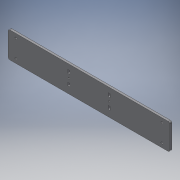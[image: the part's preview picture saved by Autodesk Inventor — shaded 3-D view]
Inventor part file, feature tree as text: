
AUTODESK INVENTOR PART (.ipt)
format: ipt  version: 2019 (Build 230136000, 136)  size: 161,280 bytes
history: native  units: in
note: dims shown in document units (in); Inventor stores cm internally (conversion verified against a paired STEP export)
features: reference x12, other x6, extrude x3, sketch x2, fillet x1, helix x1
ambient origin geometry x8: Origin, YZ Plane, XZ Plane, XY Plane, X Axis, Y Axis, Z Axis, Center Point
bodies: Solid1 (feature_tree)
feature tree (25):
  extrude  "Extrusion1"  Depth=0.1575in TaperAngle=0.0deg
  fillet  "Fillet1"  Radius=0.125in
  extrude  "Extrusion2"  Depth=0.1575in
  extrude  "Extrusion3"  Depth=0.1575in
  reference  "Reference1"
  sketch  "Sketch2"  dims[d0=1.9685in d1=0.1575in d2=0.0in d3=0.125in]
  reference  "Reference3"
  reference  "Reference4"
  reference  "Reference5"
  reference  "Reference6"
  reference  "Reference7"
  reference  "Reference8"
  reference  "Reference9"
  reference  "Reference10"
  sketch  "Sketch3"  dims[d4=0.0079in d5=0.0079in d6=0.0079in d7=0.0079in d8=0.126in d9=0.126in d10=0.1575in d11=0.0in d12=0.315in d13=0.315in d14=0.1575in d15=0.1575in d16=0.1575in d17=0.1575in d18=0.1575in d19=0.0in]
  reference  "Reference11"
  reference  "Reference12"
  reference  "Reference13"
  other  "<userpath>\Documents\CAD Files\Helix DLP\Helix DLP.iam"
  helix  "Helix DLP.iam"  [1 undecoded]
  other  "30X30 - T-slot - Aluminium Profile:1"
  other  "motor_brace_3:2"
  other  "motor_brace_3:1"
  other  "M1173041- NEMA 17 Screw rod:1"
  other  "30X30 - T-slot - Aluminium Profile:2"
note: 1 required parameter value undecoded (feature->parameter linkage not recoverable at this tier; creation-order binding heuristic only, values carry confidence <= 0.55)
